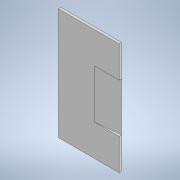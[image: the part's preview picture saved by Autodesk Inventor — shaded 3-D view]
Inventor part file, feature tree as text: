
AUTODESK INVENTOR PART (.ipt)
format: ipt  version: 2021 (Build 250183000, 183)  size: 107,008 bytes
history: native  units: mm
features: extrude x2, sketch x2, other x1
ambient origin geometry x8: Origin, YZ Plane, XZ Plane, XY Plane, X Axis, Y Axis, Z Axis, Center Point
bodies: Body1 (feature_tree)
feature tree (5):
  other  "ソリッド1"
  extrude  "押し出し1"  Depth=100.0mm TaperAngle=0.0deg
  extrude  "押し出し4"  Depth=2500.0mm
  sketch  "スケッチ1"
  sketch  "スケッチ4"
